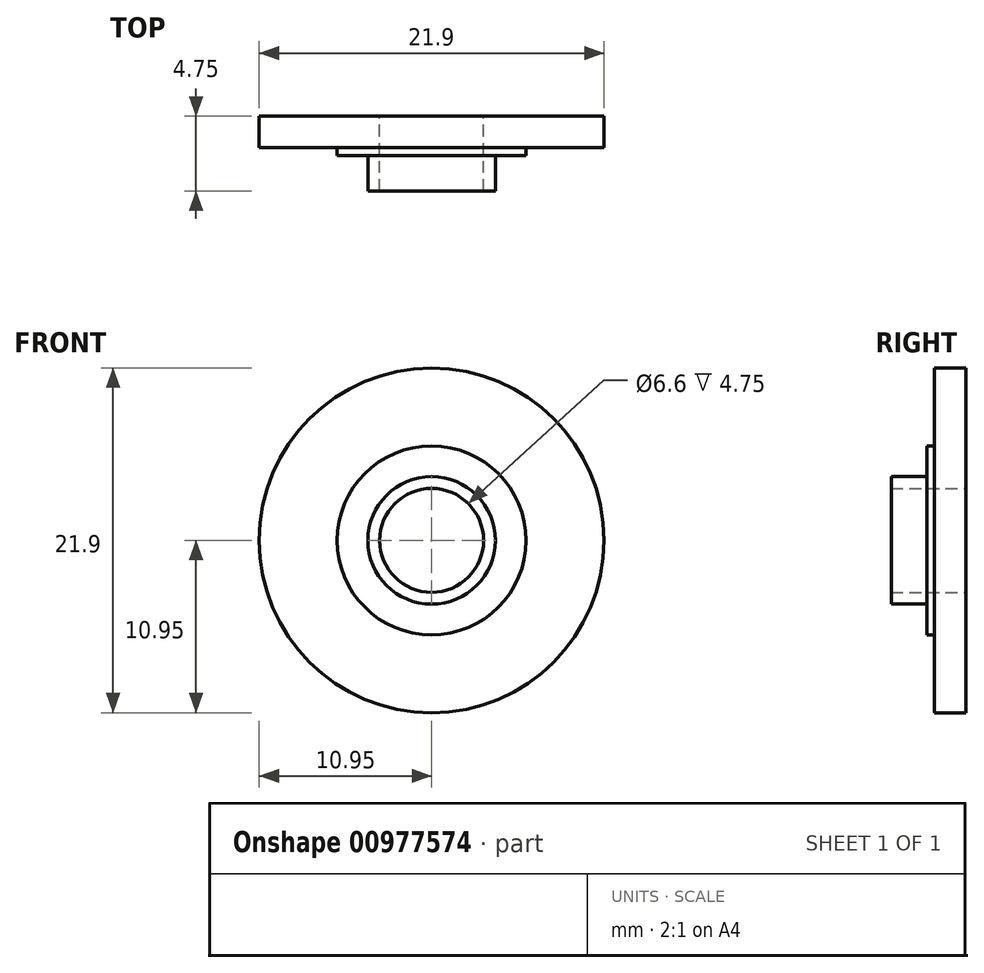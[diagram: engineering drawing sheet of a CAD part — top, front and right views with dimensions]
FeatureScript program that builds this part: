
annotation { "Feature Type Name" : "Feature", "Feature Type Description" : "" }
export const myFeature = defineFeature(function(context is Context, id is Id, definition is map)
    precondition{}
    {
        {
            var Q0;
            Q0=qCreatedBy(makeId("Front.planeOp"),FACE);
            var sketch = newSketch(context, id + "F0", { "sketchPlane" : qUnion([Q0])});
            skCircle(sketch, "E0", {"center": v(0, 0) * mm, "radius": 7.95 * mm});
            skCircle(sketch, "E1.0", {"center": v(0, 0) * mm, "radius": 10.95 * mm});
            skCircle(sketch, "E2", {"center": v(0, 0) * mm, "radius": 3.3 * mm});
            skCircle(sketch, "E3", {"center": v(0, 0) * mm, "radius": 4.05 * mm});
            skCircle(sketch, "E4", {"center": v(0, 0) * mm, "radius": 6 * mm});
            skSolve(sketch);
        }
        {
            var Q0;
            Q0=makeQuery(id+"F0.imprint","IMPRINT",FACE,{"disambiguationData":[TD([[makeQuery(id+"F0.imprint","IMPRINT",EDGE,{"derivedFrom":sQuery(id+"F0.wireOp",EDGE,"E0")}),-1.0]])]});
            extrude(context, id + "F1", {"entities" : qUnion([Q0]), "depth" : 2 * mm, "offsetDistance" : 25 * mm});
        }
        {
            var Q0;
            Q0=makeQuery(id+"F0.imprint","IMPRINT",FACE,{"disambiguationData":[TD([[makeQuery(id+"F0.imprint","IMPRINT",EDGE,{"derivedFrom":sQuery(id+"F0.wireOp",EDGE,"E0")}),1.0]])]});
            extrude(context, id + "F2", {"entities" : qUnion([Q0]), "operationType" : NewBodyOperationType.ADD, "depth" : 2 * mm, "offsetDistance" : 25 * mm});
        }
        {
            var Q0;
            Q0=makeQuery(id+"F0.imprint","IMPRINT",FACE,{"disambiguationData":[TD([[makeQuery(id+"F0.imprint","IMPRINT",EDGE,{"derivedFrom":sQuery(id+"F0.wireOp",EDGE,"E3")}),-1.0]])]});
            extrude(context, id + "F3", {"entities" : qUnion([Q0]), "operationType" : NewBodyOperationType.ADD, "depth" : 2.5 * mm, "offsetDistance" : 25 * mm});
        }
        {
            var Q0;
            Q0=makeQuery(id+"F0.imprint","IMPRINT",FACE,{"disambiguationData":[TD([[makeQuery(id+"F0.imprint","IMPRINT",EDGE,{"derivedFrom":sQuery(id+"F0.wireOp",EDGE,"E2")}),-1.0]])]});
            extrude(context, id + "F4", {"entities" : qUnion([Q0]), "operationType" : NewBodyOperationType.ADD, "depth" : 4.75 * mm, "offsetDistance" : 25 * mm});
        }
    });
